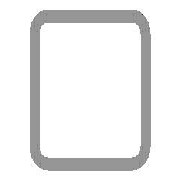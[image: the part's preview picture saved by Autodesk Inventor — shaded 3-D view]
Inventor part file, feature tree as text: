
AUTODESK INVENTOR PART (.ipt)
format: ipt  version: 2025 (Build 290162010, 162A)  size: 128,000 bytes
history: native  units: mm (DEFAULTED — no unit token found)
features: other x3, sketch x1, plane x1
ambient origin geometry x8: Origin, YZ Plane, XZ Plane, XY Plane, X Axis, Y Axis, Z Axis, Center Point
bodies: Solid1 (feature_tree), Body (feature_tree)
feature tree (5):
  other  "Driven Length"
  other  "Start plane"
  other  "End plane"
  sketch  "Sketch3"  dims[d3=8080.0mm d4=0.0mm d7=4.0mm d9=50.0mm d11=50.0mm d12=2.0mm d13=-0.0mm d14=8080.0mm d15=25.0mm d16=25.0mm d17=90.0deg d18=8080.0mm]
  plane  "Work Plane3"
